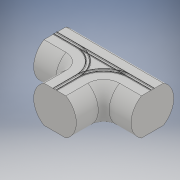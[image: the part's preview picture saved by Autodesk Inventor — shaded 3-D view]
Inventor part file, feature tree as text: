
AUTODESK INVENTOR PART (.ipt)
format: ipt  version: 2017 (Build 210142000, 142)  size: 426,496 bytes
history: native  units: in
note: dims shown in document units (in); Inventor stores cm internally (conversion verified against a paired STEP export)
features: sketch x7, extrude x4, sweep x2, plane x1, mirror x1
ambient origin geometry x8: Origin, YZ Plane, XZ Plane, XY Plane, X Axis, Y Axis, Z Axis, Center Point
bodies: Solid1 (feature_tree)
feature tree (15):
  sketch  "Sketch1"  dims[d0=6.6667in d2=9.7746in d3=4.0in d4=0.0in d5=-4.8873in]
  extrude  "corridor"  [1 undecoded]
  plane  "Work Plane1"
  sketch  "Sketch4"  dims[d6=6.6667in d10=4.0in d11=0.0in d20=0.0in d21=0.0in]
  extrude  "T bottom"  TaperAngle=0.0deg  [1 undecoded]
  sketch  "Sketch8"  dims[d171=4.8873in]
  sketch  "Sketch7"  dims[d22=4.8873in d23=0.0in]
  sweep  "corner curve"
  sketch  "Sketch9"  dims[d187=4.0in d188=0.5833in d189=3.8873in d190=3.8873in d191=1.7083in d192=0.0625in d193=0.0625in d194=1.6458in d195=0.25in d196=0.125in d198=0.0884in d199=45.0deg d200=3.3333in d201=0.125in]
  extrude  "flat of T"  TaperAngle=0.0deg  [1 undecoded]
  mirror  "Mirror parts"
  sweep  "corner curve 2"
  extrude  "hole fill in"  [1 undecoded]
  sketch  "Sketch17"  dims[d202=4.0in d203=0.5833in d204=3.8873in d205=3.8873in d206=1.7083in d207=0.0625in d208=0.0625in d209=1.6458in d210=0.25in d211=0.125in d213=0.0884in d214=45.0deg d215=3.3333in d216=0.125in d217=0.0in d218=0.0in]
  sketch  "Sketch19"  dims[d219=1.0in d220=0.0in]
note: 4 required parameter values undecoded (feature->parameter linkage not recoverable at this tier; creation-order binding heuristic only, values carry confidence <= 0.55)
